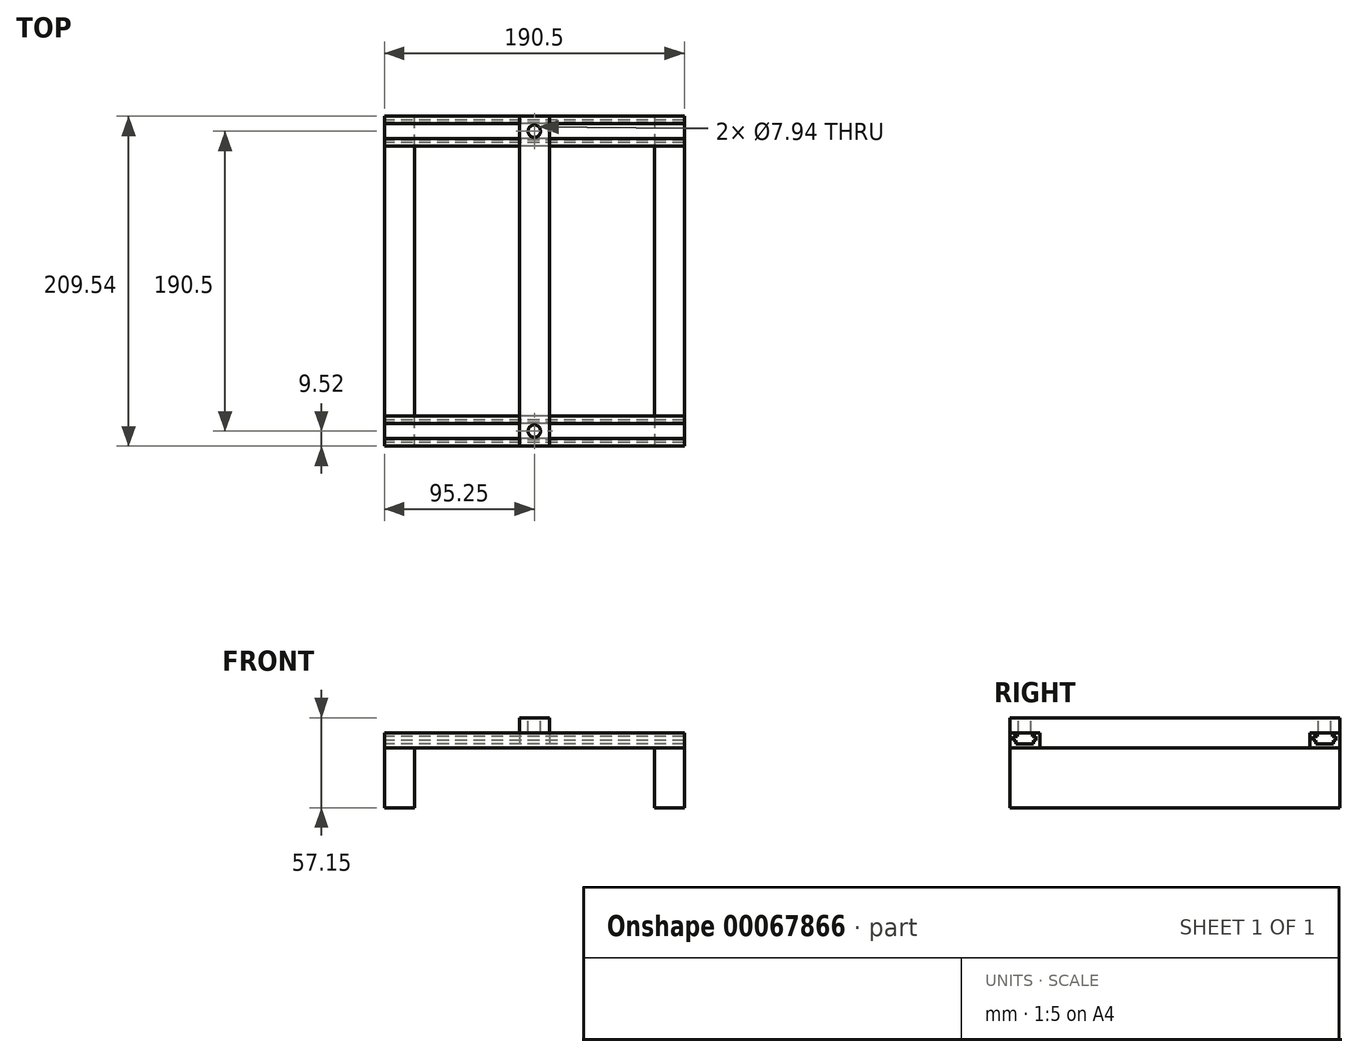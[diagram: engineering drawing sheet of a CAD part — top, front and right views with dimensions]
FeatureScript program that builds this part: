
annotation { "Feature Type Name" : "Feature", "Feature Type Description" : "" }
export const myFeature = defineFeature(function(context is Context, id is Id, definition is map)
    precondition{}
    {
        {
            var Q0;
            Q0=qCreatedBy(makeId("Right.planeOp"),FACE);
            var sketch = newSketch(context, id + "F0", { "sketchPlane" : qUnion([Q0])});
            skLineSegment(sketch, "E0", {"start": v(-100.01, 9.53) * mm, "end": v(-104.78, 9.53) * mm});
            skLineSegment(sketch, "E1", {"start": v(-104.78, 9.52) * mm, "end": v(-104.78, 0) * mm});
            skLineSegment(sketch, "E2", {"start": v(-104.78, 0) * mm, "end": v(-85.73, 0) * mm});
            skLineSegment(sketch, "E3", {"start": v(-85.73, 0) * mm, "end": v(-85.73, 9.52) * mm});
            skLineSegment(sketch, "E4", {"start": v(-85.73, 9.53) * mm, "end": v(-90.49, 9.53) * mm});
            skLineSegment(sketch, "E5", {"start": v(-90.49, 9.52) * mm, "end": v(-90.49, 7.14) * mm});
            skLineSegment(sketch, "E6", {"start": v(-90.49, 7.14) * mm, "end": v(-88.1, 7.14) * mm});
            skLineSegment(sketch, "E7", {"start": v(-88.1, 7.14) * mm, "end": v(-88.1, 4.76) * mm});
            skLineSegment(sketch, "E8", {"start": v(-88.1, 4.76) * mm, "end": v(-89.7, 4.76) * mm});
            skLineSegment(sketch, "E9", {"start": v(-89.7, 4.76) * mm, "end": v(-89.7, 2.38) * mm});
            skLineSegment(sketch, "E10", {"start": v(-89.7, 2.38) * mm, "end": v(-100.8, 2.38) * mm});
            skLineSegment(sketch, "E11", {"start": v(-100.8, 2.38) * mm, "end": v(-100.8, 4.76) * mm});
            skLineSegment(sketch, "E12", {"start": v(-100.8, 4.76) * mm, "end": v(-102.4, 4.76) * mm});
            skLineSegment(sketch, "E13", {"start": v(-102.4, 4.76) * mm, "end": v(-102.4, 7.14) * mm});
            skLineSegment(sketch, "E14", {"start": v(-102.4, 7.14) * mm, "end": v(-100.01, 7.14) * mm});
            skLineSegment(sketch, "E15", {"start": v(-100.01, 7.14) * mm, "end": v(-100.01, 9.52) * mm});
            skLineSegment(sketch, "E16", {"start": v(-95.25, 0) * mm, "end": v(95.25, 0) * mm, "construction": true});
            skLineSegment(sketch, "E17", {"start": v(90.49, 9.53) * mm, "end": v(85.73, 9.53) * mm});
            skLineSegment(sketch, "E18", {"start": v(85.73, 9.53) * mm, "end": v(85.73, 0) * mm});
            skLineSegment(sketch, "E19", {"start": v(85.73, 0) * mm, "end": v(104.78, 0) * mm});
            skLineSegment(sketch, "E20", {"start": v(104.78, 0) * mm, "end": v(104.78, 9.53) * mm});
            skLineSegment(sketch, "E21", {"start": v(104.78, 9.53) * mm, "end": v(100.01, 9.53) * mm});
            skLineSegment(sketch, "E22", {"start": v(100.01, 9.53) * mm, "end": v(100.01, 7.14) * mm});
            skLineSegment(sketch, "E23", {"start": v(100.01, 7.14) * mm, "end": v(102.4, 7.14) * mm});
            skLineSegment(sketch, "E24", {"start": v(102.4, 7.14) * mm, "end": v(102.4, 4.76) * mm});
            skLineSegment(sketch, "E25", {"start": v(102.4, 4.76) * mm, "end": v(100.8, 4.76) * mm});
            skLineSegment(sketch, "E26", {"start": v(100.8, 4.76) * mm, "end": v(100.8, 2.38) * mm});
            skLineSegment(sketch, "E27", {"start": v(100.8, 2.38) * mm, "end": v(89.7, 2.38) * mm});
            skLineSegment(sketch, "E28", {"start": v(89.7, 2.38) * mm, "end": v(89.7, 4.76) * mm});
            skLineSegment(sketch, "E29", {"start": v(89.7, 4.76) * mm, "end": v(88.1, 4.76) * mm});
            skLineSegment(sketch, "E30", {"start": v(88.1, 4.76) * mm, "end": v(88.1, 7.14) * mm});
            skLineSegment(sketch, "E31", {"start": v(88.1, 7.14) * mm, "end": v(90.49, 7.14) * mm});
            skLineSegment(sketch, "E32", {"start": v(90.49, 7.14) * mm, "end": v(90.49, 9.53) * mm});
            skSolve(sketch);
        }
        {
            var Q0;
            Q0=makeQuery(id+"F0.imprint","IMPRINT",FACE,{"disambiguationData":[TD([[makeQuery(id+"F0.imprint","IMPRINT",EDGE,{"derivedFrom":sQuery(id+"F0.wireOp",EDGE,"E0")}),1.0]])]});
            var Q1;
            Q1=makeQuery(id+"F0.imprint","IMPRINT",FACE,{"disambiguationData":[TD([[makeQuery(id+"F0.imprint","IMPRINT",EDGE,{"derivedFrom":sQuery(id+"F0.wireOp",EDGE,"E17")}),1.0]])]});
            extrude(context, id + "F3", {"entities" : qUnion([Q0, Q1]), "endBound" : BoundingType.SYMMETRIC, "depth" : 190.5 * mm});
        }
        {
            var Q0;
            Q0=makeQuery(id+"F3.opExtrude","SWEPT_FACE",FACE,{"disambiguationData":[OSD([sQuery(id+"F0.wireOp",EDGE,"E2")])]});
            var sketch = newSketch(context, id + "F1", { "sketchPlane" : qUnion([Q0])});
            skLineSegment(sketch, "E33.left", {"start": v(-95.25, 104.78) * mm, "end": v(-95.25, -104.78) * mm});
            skLineSegment(sketch, "E33.right", {"start": v(95.25, 104.78) * mm, "end": v(95.25, -104.78) * mm});
            skLineSegment(sketch, "E34", {"start": v(-95.25, 104.78) * mm, "end": v(-76.2, 104.78) * mm});
            skLineSegment(sketch, "E35", {"start": v(-76.2, 104.78) * mm, "end": v(-76.2, -104.78) * mm});
            skLineSegment(sketch, "E36", {"start": v(-76.2, -104.78) * mm, "end": v(-95.25, -104.78) * mm});
            skLineSegment(sketch, "E37", {"start": v(95.25, -104.78) * mm, "end": v(76.2, -104.78) * mm});
            skLineSegment(sketch, "E38", {"start": v(76.2, -104.78) * mm, "end": v(76.2, 104.78) * mm});
            skLineSegment(sketch, "E39", {"start": v(76.2, 104.78) * mm, "end": v(95.25, 104.78) * mm});
            skSolve(sketch);
        }
        {
            var Q0;
            Q0 = qSketchRegion(id + "F1", true);
            extrude(context, id + "F4", {"entities" : qUnion([Q0]), "depth" : 38.1 * mm});
        }
        {
            var Q0;
            Q0=qCreatedBy(makeId("Right.planeOp"),FACE);
            var sketch = newSketch(context, id + "F2", { "sketchPlane" : qUnion([Q0])});
            skLineSegment(sketch, "E40", {"start": v(0, 0) * mm, "end": v(0, 123.83) * mm, "construction": true});
            skLineSegment(sketch, "E41", {"start": v(-104.78, 9.53) * mm, "end": v(-85.73, 9.53) * mm});
            skLineSegment(sketch, "E42", {"start": v(-85.73, 9.53) * mm, "end": v(-85.73, 0) * mm});
            skLineSegment(sketch, "E43", {"start": v(-85.73, 0) * mm, "end": v(-85.73, 0) * mm});
            skLineSegment(sketch, "E44", {"start": v(104.78, 9.52) * mm, "end": v(85.73, 9.52) * mm});
            skLineSegment(sketch, "E45", {"start": v(85.73, 9.52) * mm, "end": v(85.73, 0) * mm});
            skLineSegment(sketch, "E46", {"start": v(85.73, 0) * mm, "end": v(-85.73, 0) * mm});
            skLineSegment(sketch, "E47", {"start": v(-104.78, 9.53) * mm, "end": v(-104.78, 19.05) * mm});
            skLineSegment(sketch, "E48", {"start": v(-104.78, 19.05) * mm, "end": v(104.78, 19.05) * mm});
            skLineSegment(sketch, "E49", {"start": v(104.78, 19.05) * mm, "end": v(104.78, 9.52) * mm});
            skSolve(sketch);
        }
        {
            var Q0;
            Q0 = qSketchRegion(id + "F2", true);
            extrude(context, id + "F5", {"entities" : qUnion([Q0]), "endBound" : BoundingType.SYMMETRIC, "depth" : 19.05 * mm});
        }
        {
            var Q0;
            Q0=makeQuery(id+"F5.opExtrude","SWEPT_FACE",FACE,{"disambiguationData":[OSD([sQuery(id+"F2.wireOp",EDGE,"E48")])]});
            var sketch = newSketch(context, id + "F6", { "sketchPlane" : qUnion([Q0])});
            skLineSegment(sketch, "E50", {"start": v(0, -95.25) * mm, "end": v(0, 95.25) * mm, "construction": true});
            skLineSegment(sketch, "E51", {"start": v(-9.53, 104.78) * mm, "end": v(9.53, 85.73) * mm, "construction": true});
            skSolve(sketch);
        }
        {
            var Q0;
            Q0=sQuery(id+"F6.wireOp",VERTEX,"E50.start");
            var Q1;
            Q1=sQuery(id+"F6.wireOp",VERTEX,"E50.end");
            var Q2;
            Q2=makeQuery(id+"F5.opExtrude","SWEPT_BODY",BODY,{"disambiguationData":[OSD([sQuery(id+"F2.wireOp",EDGE,"E41"),sQuery(id+"F2.wireOp",EDGE,"E42"),sQuery(id+"F2.wireOp",EDGE,"E44"),sQuery(id+"F2.wireOp",EDGE,"E45"),sQuery(id+"F2.wireOp",EDGE,"E46"),sQuery(id+"F2.wireOp",EDGE,"E47"),sQuery(id+"F2.wireOp",EDGE,"E48"),sQuery(id+"F2.wireOp",EDGE,"E49")])]});
            hole(context, id + "F7", {"style" : HoleStyle.SIMPLE, "holeDiameter" : 7.94 * mm, "endStyle" : HoleEndStyle.THROUGH, "locations" : qUnion([Q0, Q1]), "scope" : qUnion([Q2])});
        }
    });
